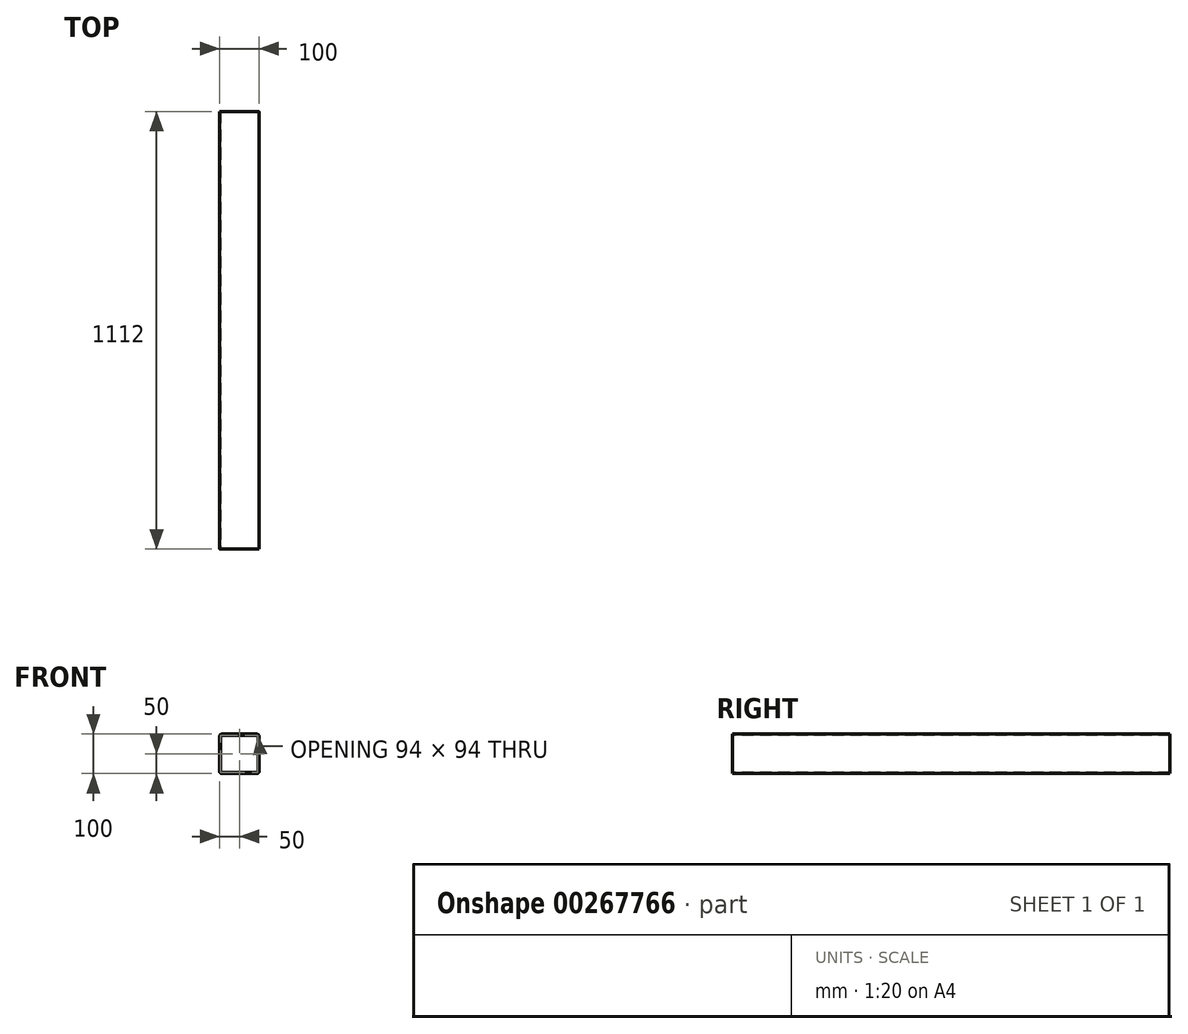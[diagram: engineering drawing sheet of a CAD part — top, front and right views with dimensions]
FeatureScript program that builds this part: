
annotation { "Feature Type Name" : "Feature", "Feature Type Description" : "" }
export const myFeature = defineFeature(function(context is Context, id is Id, definition is map)
    precondition{}
    {
        {
            var Q0;
            Q0=qCreatedBy(makeId("Front.planeOp"),FACE);
            var sketch = newSketch(context, id + "F0", { "sketchPlane" : qUnion([Q0])});
            skLineSegment(sketch, "E0.bottom", {"start": v(45, 50) * mm, "end": v(-45, 50) * mm});
            skLineSegment(sketch, "E0.top", {"start": v(45, -50) * mm, "end": v(-45, -50) * mm});
            skLineSegment(sketch, "E0.left", {"start": v(50, 45) * mm, "end": v(50, -45) * mm});
            skLineSegment(sketch, "E0.right", {"start": v(-50, 45) * mm, "end": v(-50, -45) * mm});
            skPoint(sketch, "E0.middle", {"position": v(0, 0) * mm});
            skPoint(sketch, "E1.visualSharp", {"position": v(-50, 50) * mm});
            skArc(sketch, "E1.filletArc", {"start": v(-45, 50) * mm, "mid": v(-48.54, 48.54) * mm, "end": v(-50, 45) * mm});
            skPoint(sketch, "E2.visualSharp", {"position": v(50, 50) * mm});
            skArc(sketch, "E2.filletArc", {"start": v(50, 45) * mm, "mid": v(48.54, 48.54) * mm, "end": v(45, 50) * mm});
            skPoint(sketch, "E3.visualSharp", {"position": v(50, -50) * mm});
            skArc(sketch, "E3.filletArc", {"start": v(45, -50) * mm, "mid": v(48.54, -48.54) * mm, "end": v(50, -45) * mm});
            skPoint(sketch, "E4.visualSharp", {"position": v(-50, -50) * mm});
            skArc(sketch, "E4.filletArc", {"start": v(-50, -45) * mm, "mid": v(-48.54, -48.54) * mm, "end": v(-45, -50) * mm});
            skArc(sketch, "E5.0", {"start": v(-45, 47) * mm, "mid": v(-46.41, 46.41) * mm, "end": v(-47, 45) * mm});
            skLineSegment(sketch, "E5.1", {"start": v(45, 47) * mm, "end": v(-45, 47) * mm});
            skLineSegment(sketch, "E5.2", {"start": v(-47, 45) * mm, "end": v(-47, -45) * mm});
            skArc(sketch, "E5.3", {"start": v(47, 45) * mm, "mid": v(46.41, 46.41) * mm, "end": v(45, 47) * mm});
            skArc(sketch, "E5.4", {"start": v(-47, -45) * mm, "mid": v(-46.41, -46.41) * mm, "end": v(-45, -47) * mm});
            skLineSegment(sketch, "E5.5", {"start": v(45, -47) * mm, "end": v(-45, -47) * mm});
            skArc(sketch, "E5.6", {"start": v(45, -47) * mm, "mid": v(46.41, -46.41) * mm, "end": v(47, -45) * mm});
            skLineSegment(sketch, "E5.7", {"start": v(47, 45) * mm, "end": v(47, -45) * mm});
            skSolve(sketch);
        }
        {
            var Q0;
            Q0=makeQuery(id+"F0.imprint","IMPRINT",FACE,{"disambiguationData":[TD([[makeQuery(id+"F0.imprint","IMPRINT",EDGE,{"derivedFrom":sQuery(id+"F0.wireOp",EDGE,"E0.bottom")}),1.0]])]});
            extrude(context, id + "F1", {"entities" : qUnion([Q0]), "oppositeDirection" : true, "depth" : 1112 * mm});
        }
    });
